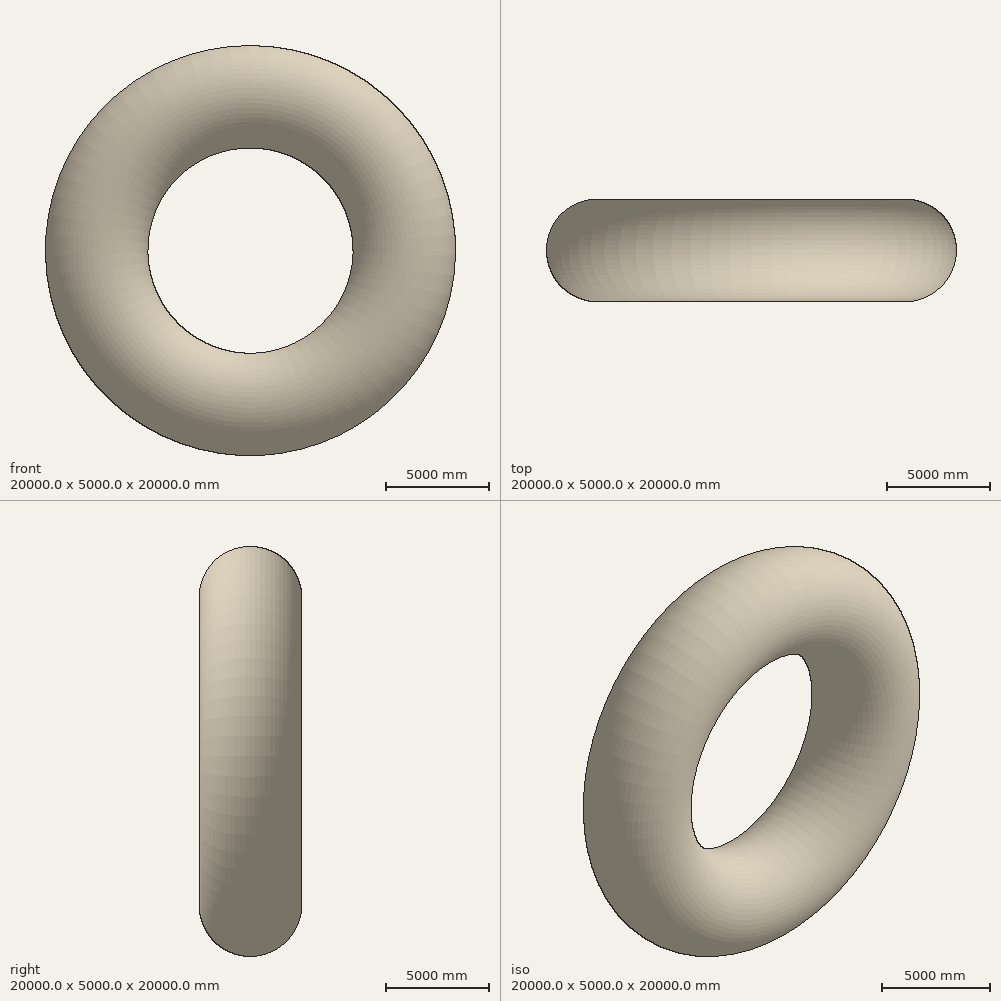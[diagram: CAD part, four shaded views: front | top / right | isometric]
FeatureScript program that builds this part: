
annotation { "Feature Type Name" : "Feature", "Feature Type Description" : "" }
export const myFeature = defineFeature(function(context is Context, id is Id, definition is map)
    precondition{}
    {
        {
            var Q0;
            Q0=qCreatedBy(makeId("Front.planeOp"),FACE);
            var sketch = newSketch(context, id + "F0", { "sketchPlane" : qUnion([Q0])});
            skCircle(sketch, "E0", {"center": v(0, 0) * mm, "radius": 7500 * mm, "construction": true});
            skPoint(sketch, "E1", {"position": v(0, 7500) * mm});
            skPoint(sketch, "E2", {"position": v(0, -7500) * mm});
            skSolve(sketch);
        }
        {
            var Q0;
            Q0=qCreatedBy(makeId("Right.planeOp"),FACE);
            var sketch = newSketch(context, id + "F1", { "sketchPlane" : qUnion([Q0])});
            skPoint(sketch, "E3.0", {"position": v(0, 7500) * mm});
            skCircle(sketch, "E4", {"center": v(0, 7500) * mm, "radius": 2500 * mm});
            skLineSegment(sketch, "E5", {"start": v(0, 0) * mm, "end": v(-7391.84, 0) * mm, "construction": true});
            skCircle(sketch, "E6.0", {"center": v(0, 7500) * mm, "radius": 2487.3 * mm});
            skSolve(sketch);
        }
        {
            var Q0;
            Q0=makeQuery(id+"F1.imprint","IMPRINT",FACE,{"disambiguationData":[TD([[makeQuery(id+"F1.imprint","IMPRINT",EDGE,{"derivedFrom":sQuery(id+"F1.wireOp",EDGE,"E4")}),1.0]])]});
            var Q1;
            Q1=sQuery(id+"F1.wireOp",EDGE,"E5");
            revolve(context, id + "F2", {"entities" : qUnion([Q0]), "axis" : qUnion([Q1]), "revolveType" : RevolveType.FULL});
        }
    });
